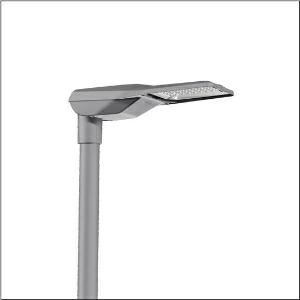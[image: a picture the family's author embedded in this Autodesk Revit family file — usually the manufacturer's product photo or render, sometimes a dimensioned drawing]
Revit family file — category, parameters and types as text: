
# Revit family: streetlight_sl_21_iq_mini___st1_5a_5xe2p31g08gb_08f7
name_source: partatom
category: Lighting Fixtures
units: mm (PartAtom-declared; Revit-internal decimal feet)

## family parameters
Cut with Voids When Loaded = No
Host = Face
Light Source = No
Part Type = Normal
Room Calculation Point = No
Round Connector Dimension = Use Diameter
Shared = No

## types (1)
- --- (1 x LED, 5580 lm, 37.1 W, 3000K)
    Apparent Load = 37 VA
    CIE Flux Codes = 22 53 95 100 100
    Color Rendering = 70
    Color Temperature = 3000K
    Default Elevation = 1800 mm
    Description = Streetlight SL 21 iQ mini, mast luminaire, primary light control with lens, of PMMA, primary optical cover: cover, of toughened safety glass, transparent, light distribution: ST1.5a, light emission: direct distribution, primary light characteristic: asymmetric, installation type: post-top, side-entry, LED, High Power LED, rated luminous flux: 5.580lm, luminous efficacy: 150lm/W, light colour: 730, colour temperature: 3000K, control: Street-Remote, Auto-Match, Temp-Guard, Lumen-Switch, Night-Set, Smart-Wire, Light-Fading, Desk-Remote (wireless, voltage-free reading and setting of iQ features in the workshop via application-optimized NFC function/RFID function), optimised constant luminous flux control (CLO 2.0), presetting dimming linear, mains connection: 220..240V, AC, 50/60Hz, start of lifetime: 37W, end of service life: 39W, reduction: 18W, luminaire housing, of diecast aluminium, powder-coated, Siteco® metallic grey (DB 702S), corrosivity category C5 mid according to DIN EN ISO 12944, please order mast flange separately, inclination adjustable: 0°, 5°, 10°, 15°, sealing non-destructively replaceable, multi-level sealing system, length: 628mm, width: 235mm, height: 110mm, mast flange for spigot size: 42mm (side-entry): 5XC10008XM4, 60/48mm (side-entry/post-top): 5XC10108XM2, 76/60mm (side-entry/post-top): 5XC10108XM1, protection rating (complete): IP66, insulation class (complete): insulation class II (safety insulation), certification: CE, ENEC, ENEC+, VDE, impact resistance: IK09, permissible operating ambient temperature for outdoor applications: -40..+50°C, standard-compliant lighting for roads and squares, packaging unit: 1 piece

Light Distribution: ST1.5a
    Height = 110 mm
    Lamp = 1 x LED
    Lamp Light Flux = 5580 lm
    Lamp Power = 37.1 W
    Lamp count = 1
    Length = 625 mm
    Luminous efficacy = 150 lm/W
    Manufacturer = Siteco
    ModVariant = No
    Model = 5XE2P31G08GB
    Number of Poles = 1
    OnlyDefault = Yes
    Power Factor = 1
    Product Name = Streetlight SL 21 iQ mini | ST1.5a
    Product group = mast luminaire | pylon top
    ProductGroupID = 6100
    Protection Class = Protection class II
    Protection Degree = IP 66
    RLX_Detail_Level = 1
    RLX_Emergency_Light_Flux = 0 lm
    RLX_Emergency_Type = 0
    RLX_Emergency_Type_DB = No
    RlxData = <blob elided: 95665 chars, md5=6f6aa433>
    Socket = socket
    Standby Power = 0 W
    System Light Flux = 5580 lm
    System Power = 37 W
    Type Comments = factory setting: luminous flux: 100 % | dim-lin: 254 | 385 mA
    Type Image = l_1003519.jpg
    URL = http://relux.com
    VarID = @adj_109049
    Voltage = 0 V
    Weight = 0.00 kg
    Width = 234 mm

## geometry (parser evidence)
native form markers: Blend x4, Sweep x11
no freeform markers — native parametric forms only
